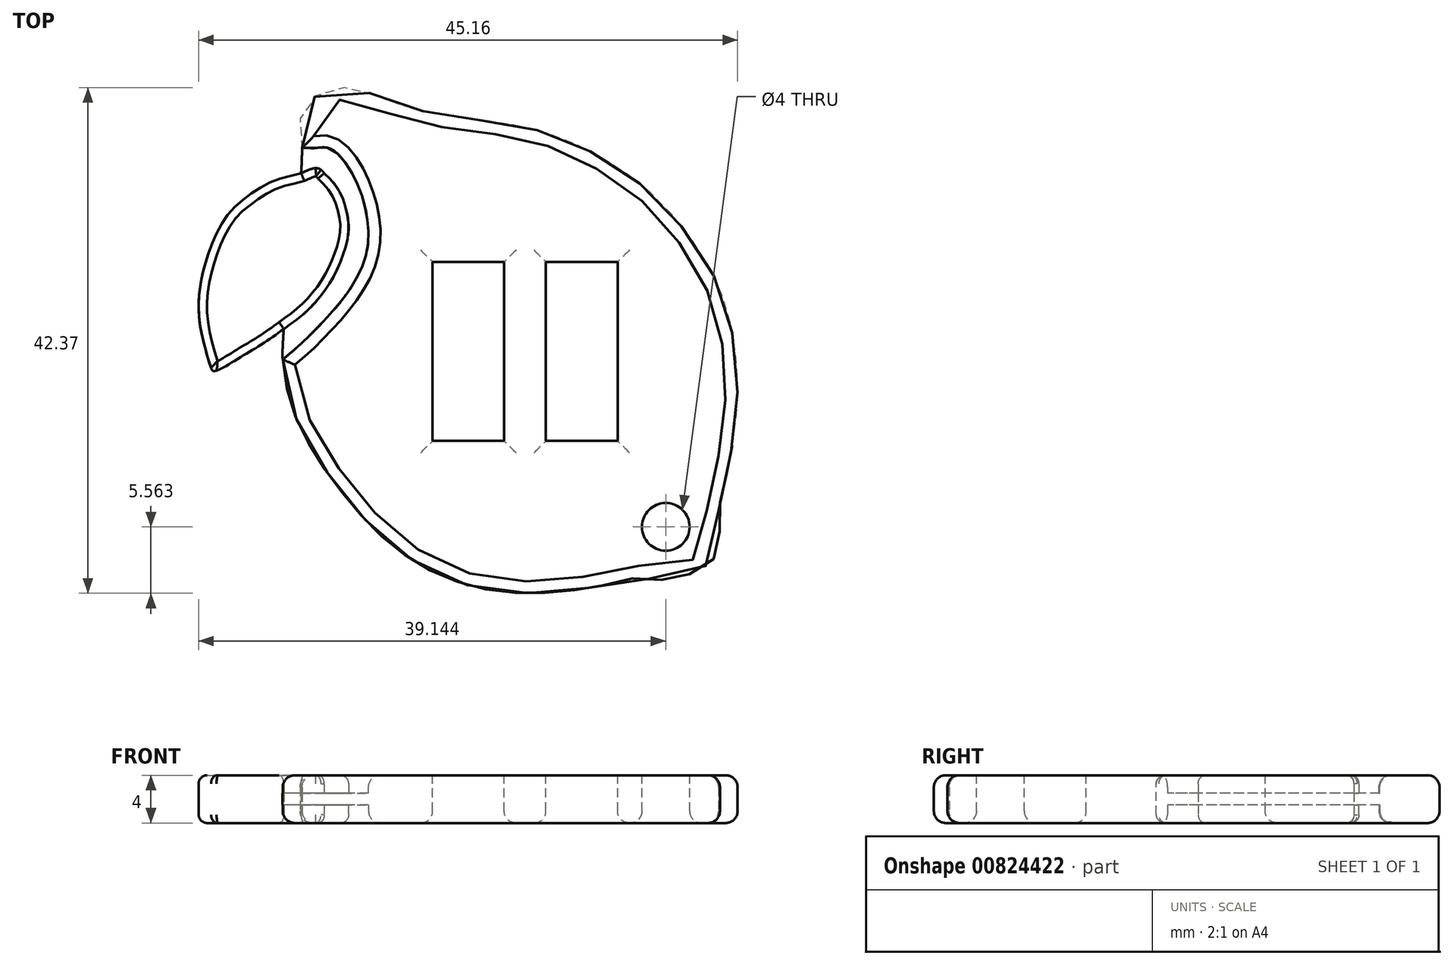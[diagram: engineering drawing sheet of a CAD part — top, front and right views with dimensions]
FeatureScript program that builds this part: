
annotation { "Feature Type Name" : "Feature", "Feature Type Description" : "" }
export const myFeature = defineFeature(function(context is Context, id is Id, definition is map)
    precondition{}
    {
        {
            var Q0;
            Q0=qCreatedBy(makeId("Top.planeOp"),FACE);
            var sketch = newSketch(context, id + "F0", { "sketchPlane" : qUnion([Q0])});
            skFitSpline(sketch, "E0", {"points": [v(-16.36, -8.62) * mm, v(-15.15, -12.65) * mm, v(-11.41, -18.47) * mm, v(-6.4, -23.46) * mm, v(0, -26.34) * mm, v(7.13, -26.58) * mm, v(12.24, -25.67) * mm, v(13.25, -25.48) * mm, v(15.13, -25.63) * mm, v(17.58, -25.16) * mm, v(19.71, -23.72) * mm, v(20.12, -21.73) * mm, v(20, -20.2) * mm, v(20.09, -19.38) * mm, v(20.96, -15.46) * mm, v(21.57, -10.63) * mm, v(21.37, -6.18) * mm, v(20.04, -1.1) * mm, v(17.46, 3.26) * mm, v(13.97, 7.1) * mm, v(9.54, 10.1) * mm, v(5.96, 11.69) * mm, v(2.17, 12.59) * mm, v(-1.63, 13.09) * mm, v(-3.73, 13.4) * mm, v(-6.45, 14.1) * mm, v(-9.4, 15.2) * mm, v(-10.76, 15.57) * mm, v(-11.94, 15.57) * mm, v(-13.09, 15.27) * mm, v(-14.4, 14.41) * mm, v(-15.02, 13.5) * mm, v(-14.9, 10.54) * mm, v(-16.42, -4.61) * mm, v(-16.36, -8.62) * mm]});
            skFitSpline(sketch, "E1", {"points": [v(-16.42, -4.61) * mm, v(-18.17, -5.84) * mm, v(-19.92, -6.9) * mm, v(-21.86, -8.03) * mm, v(-22.34, -8.13) * mm, v(-22.42, -8.07) * mm, v(-22.54, -7.84) * mm, v(-22.97, -6.4) * mm, v(-23.43, -4.4) * mm, v(-23.43, -1) * mm, v(-21.64, 4.17) * mm, v(-19.68, 6.33) * mm, v(-16.91, 7.94) * mm, v(-14.98, 8.44) * mm], "startDerivative": vector(-21.06, -15.39) * mm, "endDerivative": vector(16.54, 7.04) * mm});
            skFitSpline(sketch, "E2", {"points": [v(-14.98, 8.44) * mm, v(-13.03, 8.44) * mm], "startDerivative": vector(3.04, 1.37) * mm, "endDerivative": vector(1.45, -2.02) * mm});
            skFitSpline(sketch, "E3", {"points": [v(-13.03, 8.44) * mm, v(-11.97, 7.24) * mm, v(-11.2, 5.45) * mm, v(-11, 3.51) * mm, v(-11.52, 1.47) * mm, v(-12.49, -0.62) * mm, v(-14.36, -2.98) * mm, v(-16.42, -4.61) * mm], "startDerivative": vector(9.62, -9.24) * mm, "endDerivative": vector(-13.48, -9.49) * mm});
            skFitSpline(sketch, "E4", {"points": [v(-14.9, 10.54) * mm, v(-13.84, 10.54) * mm, v(-12.66, 10.54) * mm, v(-11.37, 9.45) * mm, v(-10.1, 7.13) * mm, v(-9.35, 4) * mm, v(-9.7, 1) * mm, v(-11.6, -2.24) * mm, v(-13.58, -4.46) * mm, v(-14.9, -5.78) * mm, v(-16.52, -7.17) * mm], "startDerivative": vector(15.22, -0.7) * mm, "endDerivative": vector(-17.41, -14.54) * mm});
            skSolve(sketch);
        }
        {
            var Q0;
            {var subQ0=sQuery(id+"F0.wireOp",EDGE,"E1");Q0=makeQuery(id+"F0.imprint","IMPRINT",FACE,{"disambiguationData":[TD([[makeQuery(id+"F0.imprint","IMPRINT",EDGE,{"derivedFrom":subQ0}),-1.0]])]});}
            var Q1;
            {var subQ3=sQuery(id+"F0.wireOp",EDGE,"E2");Q1=makeQuery(id+"F0.imprint","IMPRINT",FACE,{"disambiguationData":[TD([[makeQuery(id+"F0.imprint","IMPRINT",EDGE,{"derivedFrom":subQ3}),-1.0]])]});}
            var Q2;
            {var subQ0=sQuery(id+"F0.wireOp",EDGE,"E4");Q2=makeQuery(id+"F0.imprint","IMPRINT",FACE,{"disambiguationData":[TD([[makeQuery(id+"F0.imprint","IMPRINT",EDGE,{"derivedFrom":subQ0}),1.0]])]});}
            extrude(context, id + "F1", {"entities" : qUnion([Q0, Q1, Q2]), "endBound" : BoundingType.SYMMETRIC, "depth" : 4 * mm, "offsetDistance" : 25 * mm});
        }
        {
            var Q0;
            {var subQ4=sQuery(id+"F0.wireOp",EDGE,"E2");Q0=makeQuery(id+"F0.imprint","IMPRINT",FACE,{"disambiguationData":[TD([[makeQuery(id+"F0.imprint","IMPRINT",EDGE,{"derivedFrom":subQ4}),1.0]])]});}
            extrude(context, id + "F2", {"entities" : qUnion([Q0]), "operationType" : NewBodyOperationType.ADD, "endBound" : BoundingType.SYMMETRIC, "depth" : 1 * mm, "offsetDistance" : 25 * mm});
        }
        {
            var Q0;
            Q0=makeQuery(id+"F1.opExtrude","CAP_FACE",FACE,{"disambiguationData":[OSD([sQuery(id+"F0.wireOp",EDGE,"E1"),sQuery(id+"F0.wireOp",EDGE,"E2"),sQuery(id+"F0.wireOp",EDGE,"E3")])],"isStart":false});
            var Q1;
            Q1=makeQuery(id+"F1.opExtrude","CAP_FACE",FACE,{"disambiguationData":[OSD([sQuery(id+"F0.wireOp",EDGE,"E1"),sQuery(id+"F0.wireOp",EDGE,"E2"),sQuery(id+"F0.wireOp",EDGE,"E3")])],"isStart":true});
            fillet(context, id + "F3", {"entities" : qUnion([Q0, Q1]), "radius" : .7 * mm, "tangentPropagation" : true, "allowEdgeOverflow" : false});
        }
        {
            var Q0;
            Q0=makeQuery(id+"F1.opExtrude","CAP_FACE",FACE,{"disambiguationData":[OSD([sQuery(id+"F0.wireOp",EDGE,"E0"),sQuery(id+"F0.wireOp",EDGE,"E4")])],"isStart":false});
            var Q1;
            Q1=makeQuery(id+"F1.opExtrude","CAP_FACE",FACE,{"disambiguationData":[OSD([sQuery(id+"F0.wireOp",EDGE,"E0"),sQuery(id+"F0.wireOp",EDGE,"E4")])],"isStart":true});
            fillet(context, id + "F4", {"entities" : qUnion([Q0, Q1]), "radius" : 1 * mm, "tangentPropagation" : true, "allowEdgeOverflow" : false});
        }
        {
            var Q0;
            Q0=makeQuery(id+"F1.opExtrude","CAP_FACE",FACE,{"disambiguationData":[OSD([sQuery(id+"F0.wireOp",EDGE,"E0"),sQuery(id+"F0.wireOp",EDGE,"E4")])],"isStart":false});
            var sketch = newSketch(context, id + "F5", { "sketchPlane" : qUnion([Q0])});
            skLineSegment(sketch, "E5.bottom", {"start": v(-3.96, 1) * mm, "end": v(2.04, 1) * mm});
            skLineSegment(sketch, "E5.top", {"start": v(-3.96, -14) * mm, "end": v(2.04, -14) * mm});
            skLineSegment(sketch, "E5.left", {"start": v(-3.96, 1) * mm, "end": v(-3.96, -14) * mm});
            skLineSegment(sketch, "E5.right", {"start": v(2.04, 1) * mm, "end": v(2.04, -14) * mm});
            skLineSegment(sketch, "E6.bottom", {"start": v(5.54, 1) * mm, "end": v(11.54, 1) * mm});
            skLineSegment(sketch, "E6.top", {"start": v(5.54, -14) * mm, "end": v(11.54, -14) * mm});
            skLineSegment(sketch, "E6.left", {"start": v(5.54, 1) * mm, "end": v(5.54, -14) * mm});
            skLineSegment(sketch, "E6.right", {"start": v(11.54, 1) * mm, "end": v(11.54, -14) * mm});
            skSolve(sketch);
        }
        {
            var Q0;
            Q0 = qSketchRegion(id + "F5", true);
            extrude(context, id + "F6", {"entities" : qUnion([Q0]), "operationType" : NewBodyOperationType.REMOVE, "oppositeDirection" : true, "depth" : 5 * mm, "offsetDistance" : 25 * mm});
        }
        {
            var Q0;
            Q0=makeQuery(id+"F1.opExtrude","CAP_FACE",FACE,{"disambiguationData":[OSD([sQuery(id+"F0.wireOp",EDGE,"E0"),sQuery(id+"F0.wireOp",EDGE,"E4")])],"isStart":false});
            var sketch = newSketch(context, id + "F7", { "sketchPlane" : qUnion([Q0])});
            skCircle(sketch, "E7", {"center": v(15.58, -21.2) * mm, "radius": 2 * mm});
            skSolve(sketch);
        }
        {
            var Q0;
            Q0=qSketchRegion(id+"F7",true);
            extrude(context, id + "F8", {"entities" : qUnion([Q0]), "operationType" : NewBodyOperationType.REMOVE, "oppositeDirection" : true, "depth" : 5 * mm, "offsetDistance" : 25 * mm});
        }
        {
            var Q0;
            Q0=makeQuery(id+"F6.boolean.opBoolean","COPY",EDGE,{"derivedFrom":makeQuery(id+"F6.opExtrude","CAP_EDGE",EDGE,{"disambiguationData":[OSD([sQuery(id+"F5.wireOp",EDGE,"E5.left")])],"isStart":true})});
            var Q1;
            Q1=makeQuery(id+"F6.boolean.opBoolean","COPY",EDGE,{"derivedFrom":makeQuery(id+"F6.opExtrude","CAP_EDGE",EDGE,{"disambiguationData":[OSD([sQuery(id+"F5.wireOp",EDGE,"E6.left")])],"isStart":true})});
            var Q2;
            Q2=makeQuery(id+"F6.boolean.opBoolean","COPY",EDGE,{"derivedFrom":makeQuery(id+"F6.opExtrude","CAP_EDGE",EDGE,{"disambiguationData":[OSD([sQuery(id+"F5.wireOp",EDGE,"E6.right")])],"isStart":true})});
            var Q3;
            Q3=makeQuery(id+"F6.boolean.opBoolean","COPY",EDGE,{"derivedFrom":makeQuery(id+"F6.opExtrude","CAP_EDGE",EDGE,{"disambiguationData":[OSD([sQuery(id+"F5.wireOp",EDGE,"E6.bottom")])],"isStart":true})});
            var Q4;
            Q4=makeQuery(id+"F6.boolean.opBoolean","COPY",EDGE,{"derivedFrom":makeQuery(id+"F6.opExtrude","CAP_EDGE",EDGE,{"disambiguationData":[OSD([sQuery(id+"F5.wireOp",EDGE,"E5.bottom")])],"isStart":true})});
            var Q5;
            Q5=makeQuery(id+"F6.boolean.opBoolean","COPY",EDGE,{"derivedFrom":makeQuery(id+"F6.opExtrude","CAP_EDGE",EDGE,{"disambiguationData":[OSD([sQuery(id+"F5.wireOp",EDGE,"E5.right")])],"isStart":true})});
            var Q6;
            Q6=makeQuery(id+"F6.boolean.opBoolean","COPY",EDGE,{"derivedFrom":makeQuery(id+"F6.opExtrude","CAP_EDGE",EDGE,{"disambiguationData":[OSD([sQuery(id+"F5.wireOp",EDGE,"E6.top")])],"isStart":true})});
            var Q7;
            Q7=makeQuery(id+"F6.boolean.opBoolean","COPY",EDGE,{"derivedFrom":makeQuery(id+"F6.opExtrude","CAP_EDGE",EDGE,{"disambiguationData":[OSD([sQuery(id+"F5.wireOp",EDGE,"E5.top")])],"isStart":true})});
            var Q8;
            Q8=makeQuery(id+"F8.boolean.opBoolean","COPY",EDGE,{"derivedFrom":makeQuery(id+"F8.opExtrude","CAP_EDGE",EDGE,{"disambiguationData":[OSD([sQuery(id+"F7.wireOp",EDGE,"E7")])],"isStart":true})});
            var Q9;
            Q9=makeQuery(id+"F8.boolean.opBoolean","COPY",EDGE,{"derivedFrom":makeQuery(id+"F8.opExtrude","CAP_EDGE",EDGE,{"disambiguationData":[OSD([sQuery(id+"F7.wireOp",EDGE,"E7")])],"isStart":false})});
            var Q10;
            Q10=makeQuery(id+"F6.boolean.opBoolean","COPY",EDGE,{"derivedFrom":makeQuery(id+"F6.opExtrude","CAP_EDGE",EDGE,{"disambiguationData":[OSD([sQuery(id+"F5.wireOp",EDGE,"E5.left")])],"isStart":false})});
            var Q11;
            Q11=makeQuery(id+"F6.boolean.opBoolean","COPY",EDGE,{"derivedFrom":makeQuery(id+"F6.opExtrude","CAP_EDGE",EDGE,{"disambiguationData":[OSD([sQuery(id+"F5.wireOp",EDGE,"E5.top")])],"isStart":false})});
            var Q12;
            Q12=makeQuery(id+"F6.boolean.opBoolean","COPY",EDGE,{"derivedFrom":makeQuery(id+"F6.opExtrude","CAP_EDGE",EDGE,{"disambiguationData":[OSD([sQuery(id+"F5.wireOp",EDGE,"E5.right")])],"isStart":false})});
            var Q13;
            Q13=makeQuery(id+"F6.boolean.opBoolean","COPY",EDGE,{"derivedFrom":makeQuery(id+"F6.opExtrude","CAP_EDGE",EDGE,{"disambiguationData":[OSD([sQuery(id+"F5.wireOp",EDGE,"E5.bottom")])],"isStart":false})});
            var Q14;
            Q14=makeQuery(id+"F6.boolean.opBoolean","COPY",EDGE,{"derivedFrom":makeQuery(id+"F6.opExtrude","CAP_EDGE",EDGE,{"disambiguationData":[OSD([sQuery(id+"F5.wireOp",EDGE,"E6.left")])],"isStart":false})});
            var Q15;
            Q15=makeQuery(id+"F6.boolean.opBoolean","COPY",EDGE,{"derivedFrom":makeQuery(id+"F6.opExtrude","CAP_EDGE",EDGE,{"disambiguationData":[OSD([sQuery(id+"F5.wireOp",EDGE,"E6.bottom")])],"isStart":false})});
            var Q16;
            Q16=makeQuery(id+"F6.boolean.opBoolean","COPY",EDGE,{"derivedFrom":makeQuery(id+"F6.opExtrude","CAP_EDGE",EDGE,{"disambiguationData":[OSD([sQuery(id+"F5.wireOp",EDGE,"E6.top")])],"isStart":false})});
            var Q17;
            Q17=makeQuery(id+"F6.boolean.opBoolean","COPY",EDGE,{"derivedFrom":makeQuery(id+"F6.opExtrude","CAP_EDGE",EDGE,{"disambiguationData":[OSD([sQuery(id+"F5.wireOp",EDGE,"E6.right")])],"isStart":false})});
            var Q18;
            Q18=makeQuery(id+"F6.boolean.opBoolean","INTERSECT",EDGE,{"derivedFrom":[makeQuery(id+"F1.opExtrude","CAP_FACE",FACE,{"disambiguationData":[OSD([sQuery(id+"F0.wireOp",EDGE,"E0"),sQuery(id+"F0.wireOp",EDGE,"E4")])],"isStart":true}),makeQuery(id+"F6.opExtrude","SWEPT_FACE",FACE,{"disambiguationData":[OSD([sQuery(id+"F5.wireOp",EDGE,"E5.left")])]})]});
            var Q19;
            Q19=makeQuery(id+"F6.boolean.opBoolean","INTERSECT",EDGE,{"derivedFrom":[makeQuery(id+"F1.opExtrude","CAP_FACE",FACE,{"disambiguationData":[OSD([sQuery(id+"F0.wireOp",EDGE,"E0"),sQuery(id+"F0.wireOp",EDGE,"E4")])],"isStart":true}),makeQuery(id+"F6.opExtrude","SWEPT_FACE",FACE,{"disambiguationData":[OSD([sQuery(id+"F5.wireOp",EDGE,"E5.top")])]})]});
            var Q20;
            Q20=makeQuery(id+"F6.boolean.opBoolean","INTERSECT",EDGE,{"derivedFrom":[makeQuery(id+"F1.opExtrude","CAP_FACE",FACE,{"disambiguationData":[OSD([sQuery(id+"F0.wireOp",EDGE,"E0"),sQuery(id+"F0.wireOp",EDGE,"E4")])],"isStart":true}),makeQuery(id+"F6.opExtrude","SWEPT_FACE",FACE,{"disambiguationData":[OSD([sQuery(id+"F5.wireOp",EDGE,"E5.right")])]})]});
            var Q21;
            Q21=makeQuery(id+"F6.boolean.opBoolean","INTERSECT",EDGE,{"derivedFrom":[makeQuery(id+"F1.opExtrude","CAP_FACE",FACE,{"disambiguationData":[OSD([sQuery(id+"F0.wireOp",EDGE,"E0"),sQuery(id+"F0.wireOp",EDGE,"E4")])],"isStart":true}),makeQuery(id+"F6.opExtrude","SWEPT_FACE",FACE,{"disambiguationData":[OSD([sQuery(id+"F5.wireOp",EDGE,"E6.left")])]})]});
            var Q22;
            Q22=makeQuery(id+"F6.boolean.opBoolean","INTERSECT",EDGE,{"derivedFrom":[makeQuery(id+"F1.opExtrude","CAP_FACE",FACE,{"disambiguationData":[OSD([sQuery(id+"F0.wireOp",EDGE,"E0"),sQuery(id+"F0.wireOp",EDGE,"E4")])],"isStart":true}),makeQuery(id+"F6.opExtrude","SWEPT_FACE",FACE,{"disambiguationData":[OSD([sQuery(id+"F5.wireOp",EDGE,"E6.top")])]})]});
            var Q23;
            Q23=makeQuery(id+"F6.boolean.opBoolean","INTERSECT",EDGE,{"derivedFrom":[makeQuery(id+"F1.opExtrude","CAP_FACE",FACE,{"disambiguationData":[OSD([sQuery(id+"F0.wireOp",EDGE,"E0"),sQuery(id+"F0.wireOp",EDGE,"E4")])],"isStart":true}),makeQuery(id+"F6.opExtrude","SWEPT_FACE",FACE,{"disambiguationData":[OSD([sQuery(id+"F5.wireOp",EDGE,"E6.right")])]})]});
            var Q24;
            Q24=makeQuery(id+"F6.boolean.opBoolean","INTERSECT",EDGE,{"derivedFrom":[makeQuery(id+"F1.opExtrude","CAP_FACE",FACE,{"disambiguationData":[OSD([sQuery(id+"F0.wireOp",EDGE,"E0"),sQuery(id+"F0.wireOp",EDGE,"E4")])],"isStart":true}),makeQuery(id+"F6.opExtrude","SWEPT_FACE",FACE,{"disambiguationData":[OSD([sQuery(id+"F5.wireOp",EDGE,"E5.bottom")])]})]});
            var Q25;
            Q25=makeQuery(id+"F6.boolean.opBoolean","INTERSECT",EDGE,{"derivedFrom":[makeQuery(id+"F1.opExtrude","CAP_FACE",FACE,{"disambiguationData":[OSD([sQuery(id+"F0.wireOp",EDGE,"E0"),sQuery(id+"F0.wireOp",EDGE,"E4")])],"isStart":true}),makeQuery(id+"F6.opExtrude","SWEPT_FACE",FACE,{"disambiguationData":[OSD([sQuery(id+"F5.wireOp",EDGE,"E6.bottom")])]})]});
            var Q26;
            Q26=makeQuery(id+"F8.boolean.opBoolean","INTERSECT",EDGE,{"derivedFrom":[makeQuery(id+"F1.opExtrude","CAP_FACE",FACE,{"disambiguationData":[OSD([sQuery(id+"F0.wireOp",EDGE,"E0"),sQuery(id+"F0.wireOp",EDGE,"E4")])],"isStart":true}),makeQuery(id+"F8.opExtrude","SWEPT_FACE",FACE,{"disambiguationData":[OSD([sQuery(id+"F7.wireOp",EDGE,"E7")])]})]});
            fillet(context, id + "F9", {"entities" : qUnion([Q0, Q1, Q2, Q3, Q4, Q5, Q6, Q7, Q8, Q9, Q10, Q11, Q12, Q13, Q14, Q15, Q16, Q17, Q18, Q19, Q20, Q21, Q22, Q23, Q24, Q25, Q26]), "radius" : 1 * mm, "tangentPropagation" : true, "allowEdgeOverflow" : false});
        }
    });
